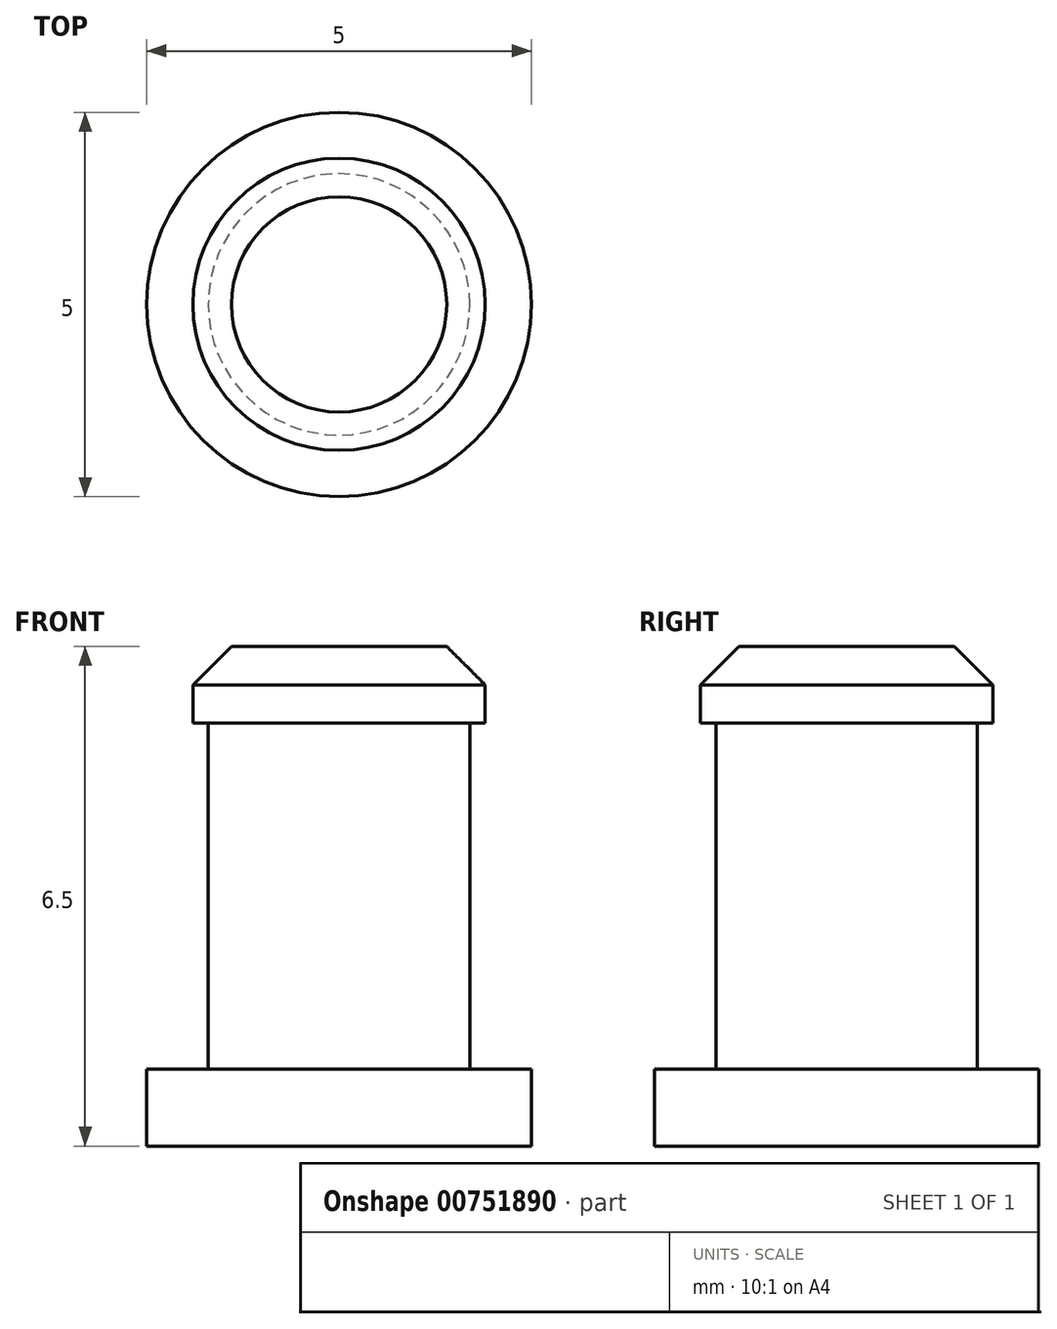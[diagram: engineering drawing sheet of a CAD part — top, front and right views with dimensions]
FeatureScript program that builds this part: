
annotation { "Feature Type Name" : "Feature", "Feature Type Description" : "" }
export const myFeature = defineFeature(function(context is Context, id is Id, definition is map)
    precondition{}
    {
        {
            var Q0;
            Q0=qCreatedBy(makeId("Top.planeOp"),FACE);
            var sketch = newSketch(context, id + "F0", { "sketchPlane" : qUnion([Q0])});
            skCircle(sketch, "E0", {"center": v(0, 0) * mm, "radius": 2.5 * mm});
            skSolve(sketch);
        }
        {
            var Q0;
            Q0 = qSketchRegion(id + "F0", true);
            extrude(context, id + "F1", {"entities" : qUnion([Q0]), "depth" : 1 * mm, "offsetDistance" : 25 * mm});
        }
        {
            var Q0;
            Q0=makeQuery(id+"F1.opExtrude","CAP_FACE",FACE,{"disambiguationData":[OSD([sQuery(id+"F0.wireOp",EDGE,"E0")])],"isStart":false});
            var sketch = newSketch(context, id + "F2", { "sketchPlane" : qUnion([Q0])});
            skCircle(sketch, "E1", {"center": v(0, 0) * mm, "radius": 1.7 * mm});
            skSolve(sketch);
        }
        {
            var Q0;
            Q0 = qSketchRegion(id + "F2", true);
            extrude(context, id + "F3", {"entities" : qUnion([Q0]), "operationType" : NewBodyOperationType.ADD, "depth" : 5.5 * mm, "offsetDistance" : 25 * mm});
        }
        {
            var Q0;
            Q0=makeQuery(id+"F3.opExtrude","CAP_FACE",FACE,{"disambiguationData":[OSD([sQuery(id+"F2.wireOp",EDGE,"E1")])],"isStart":false});
            var sketch = newSketch(context, id + "F4", { "sketchPlane" : qUnion([Q0])});
            skCircle(sketch, "E2", {"center": v(0, 0) * mm, "radius": 1.9 * mm});
            skSolve(sketch);
        }
        {
            var Q0;
            Q0 = qSketchRegion(id + "F4", true);
            extrude(context, id + "F5", {"entities" : qUnion([Q0]), "operationType" : NewBodyOperationType.ADD, "oppositeDirection" : true, "depth" : 1 * mm, "offsetDistance" : 25 * mm});
        }
        {
            var Q0;
            Q0=makeQuery(id+"F5.opExtrude","CAP_EDGE",EDGE,{"disambiguationData":[OSD([sQuery(id+"F4.wireOp",EDGE,"E2")])],"isStart":true});
            chamfer(context, id + "F6", {"entities" : qUnion([Q0]), "width" : 0.5 * mm, "tangentPropagation" : true});
        }
    });
